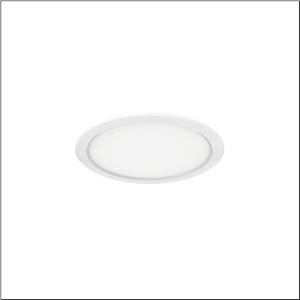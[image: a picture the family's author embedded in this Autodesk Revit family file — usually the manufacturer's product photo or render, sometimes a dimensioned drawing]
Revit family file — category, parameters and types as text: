
# Revit family: lunis_41_eco_51ds107f34a
name_source: partatom
category: Lighting Fixtures
units: mm (PartAtom-declared; Revit-internal decimal feet)

## family parameters
Cut with Voids When Loaded = No
Host = Face
Light Source = No
Part Type = Normal
Room Calculation Point = No
Round Connector Dimension = Use Diameter
Shared = No

## types (1)
- Lunis 41 ECO (1 x LED, 2200 lm, 22 W, 3000K)
    Apparent Load = 22 VA
    CIE Flux Codes = 47 80 97 100 100
    Color Rendering = 80
    Color Temperature = 3000K
    Default Elevation = 1800 mm
    Description = Lunis 41,  ECO, downlight, light emission: direct distribution, LED rated luminous flux: 2.200lm, light colour: 830, control gear: ECG, mains connection: 230V, AC, 50/60Hz, housing, round, of aluminium, coated, traffic white (RAL 9016), diameter: 216mm, recess depth: 58mm, protection rating (complete): IP20, protection rating (on room side): IP40, insulation class (complete): insulation class II (safety insulation), certification: CE, permissible ambient temperature for indoor applications: -20..+40°C, packaging unit: 1 piece
    Height = 0 mm  [stored 0 ft]
    Lamp = 1 x LED
    Lamp Light Flux = 2200 lm
    Lamp Power = 22 W
    Lamp count = 1
    Length = 216 mm
    Luminous efficacy = 100 lm/W
    Manufacturer = Siteco
    ModVariant = No
    Model = 51DS107F34A
    Mounting Place = Ceiling
    Mounting Type = Recessed
    Number of Poles = 1
    OnlyDefault = Yes
    Power Factor = 1
    Product Name = Lunis 41 ECO
    Product group = downlight
    ProductGroupID = 400
    Protection Class = Protection class II
    Protection Degree = IP 20
    RLX_Detail_Level = 1
    RLX_Emergency_Light_Flux = 0 lm
    RLX_Emergency_Type = 0
    RLX_Emergency_Type_DB = No
    RlxData = <blob elided: 22801 chars, md5=428b0442>
    Socket = socket
    Standby Power = 0 W
    System Light Flux = 2200 lm
    System Power = 22 W
    Type Comments = Product without accessories
    Type Image = l_1007043.jpg
    URL = http://relux.com
    VarID = ---
    Voltage = 0 V
    Weight = 0.00 kg
    Width = 0 mm  [stored 0 ft]

note: [stored X ft] marks values corroborated as IEEE doubles in the binary element streams (Revit-internal decimal feet)

## geometry (parser evidence)
native form markers: Blend x4, Sweep x13
no freeform markers — native parametric forms only
